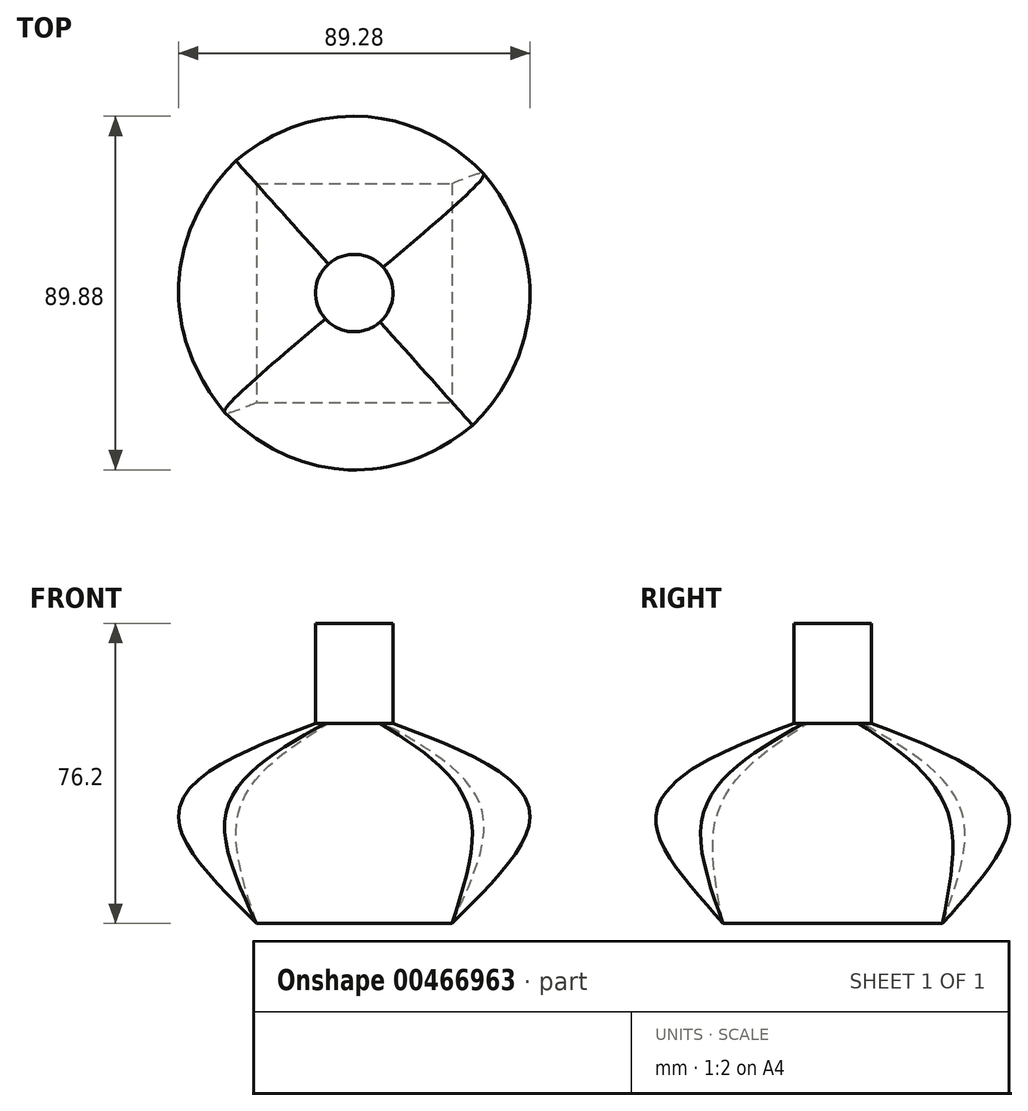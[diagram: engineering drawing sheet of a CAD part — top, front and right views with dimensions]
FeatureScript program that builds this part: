
annotation { "Feature Type Name" : "Feature", "Feature Type Description" : "" }
export const myFeature = defineFeature(function(context is Context, id is Id, definition is map)
    precondition{}
    {
        {
            var Q0;
            Q0=qCreatedBy(makeId("Top.planeOp"),FACE);
            var sketch = newSketch(context, id + "F0", { "sketchPlane" : qUnion([Q0])});
            skLineSegment(sketch, "E0.bottom", {"start": v(-24.84, 27.87) * mm, "end": v(24.84, 27.87) * mm});
            skLineSegment(sketch, "E0.top", {"start": v(-24.84, -27.87) * mm, "end": v(24.84, -27.87) * mm});
            skLineSegment(sketch, "E0.left", {"start": v(-24.84, 27.87) * mm, "end": v(-24.84, -27.87) * mm});
            skLineSegment(sketch, "E0.right", {"start": v(24.84, 27.87) * mm, "end": v(24.84, -27.87) * mm});
            skPoint(sketch, "E0.middle", {"position": v(0, 0) * mm});
            skSolve(sketch);
        }
        {
            var Q0;
            Q0=qCreatedBy(makeId("Top.planeOp"),FACE);
            cPlane(context, id + "F1", {"entities" : qUnion([Q0]), "cplaneType" : CPlaneType.OFFSET, "offset" : 25.4 * mm, "width" : 152.4 * mm, "height" : 152.4 * mm});
        }
        {
            var Q0;
            Q0=qCreatedBy(id+"F1.planeOp",FACE);
            var sketch = newSketch(context, id + "F2", { "sketchPlane" : qUnion([Q0])});
            skEllipse(sketch, "E1", {"center": v(0, 0) * mm, "majorRadius": 44.44 * mm, "minorRadius": 44.94 * mm, "majorAxis": v(0.95, 0.3)});
            skSolve(sketch);
        }
        {
            var Q0;
            Q0=qCreatedBy(id+"F1.planeOp",FACE);
            cPlane(context, id + "F3", {"entities" : qUnion([Q0]), "cplaneType" : CPlaneType.OFFSET, "offset" : 25.4 * mm, "width" : 152.4 * mm, "height" : 152.4 * mm});
        }
        {
            var Q0;
            Q0=qCreatedBy(id+"F3.planeOp",FACE);
            var sketch = newSketch(context, id + "F4", { "sketchPlane" : qUnion([Q0])});
            skCircle(sketch, "E2", {"center": v(0, 0) * mm, "radius": 9.84 * mm});
            skSolve(sketch);
        }
        {
            var Q0;
            Q0=makeQuery(id+"F0.imprint","IMPRINT",FACE,{"disambiguationData":[TD([[makeQuery(id+"F0.imprint","IMPRINT",EDGE,{"derivedFrom":sQuery(id+"F0.wireOp",EDGE,"E0.bottom")}),-1.0]])]});
            var Q1;
            Q1=makeQuery(id+"F2.imprint","IMPRINT",FACE,{"disambiguationData":[TD([[makeQuery(id+"F2.imprint","IMPRINT",EDGE,{"derivedFrom":sQuery(id+"F2.wireOp",EDGE,"E1")}),1.0]])]});
            var Q2;
            Q2=makeQuery(id+"F4.imprint","IMPRINT",FACE,{"disambiguationData":[TD([[makeQuery(id+"F4.imprint","IMPRINT",EDGE,{"derivedFrom":sQuery(id+"F4.wireOp",EDGE,"E2")}),1.0]])]});
            loft(context, id + "F5", {"sheetProfilesArray" : [{ "sheetProfileEntities" : qUnion([Q0]) }, { "sheetProfileEntities" : qUnion([Q1]) }, { "sheetProfileEntities" : qUnion([Q2]) }]});
        }
        {
            var Q0;
            Q0=makeQuery(id+"F5.opLoft","CAP_FACE",FACE,{"disambiguationData":[OSD([makeQuery(id+"F4.imprint","IMPRINT",FACE,{"disambiguationData":[TD([[makeQuery(id+"F4.imprint","IMPRINT",EDGE,{"derivedFrom":sQuery(id+"F4.wireOp",EDGE,"E2")}),1.0]])]})])],"isStart":true});
            extrude(context, id + "F6", {"entities" : qUnion([Q0]), "operationType" : NewBodyOperationType.ADD, "oppositeDirection" : true, "depth" : 8.13 * mm});
        }
        {
            var Q0;
            Q0=makeQuery(id+"F5.opLoft","CAP_FACE",FACE,{"disambiguationData":[OSD([makeQuery(id+"F4.imprint","IMPRINT",FACE,{"disambiguationData":[TD([[makeQuery(id+"F4.imprint","IMPRINT",EDGE,{"derivedFrom":sQuery(id+"F4.wireOp",EDGE,"E2")}),1.0]])]})])],"isStart":true});
            extrude(context, id + "F7", {"entities" : qUnion([Q0]), "operationType" : NewBodyOperationType.ADD, "depth" : 25.4 * mm});
        }
    });
